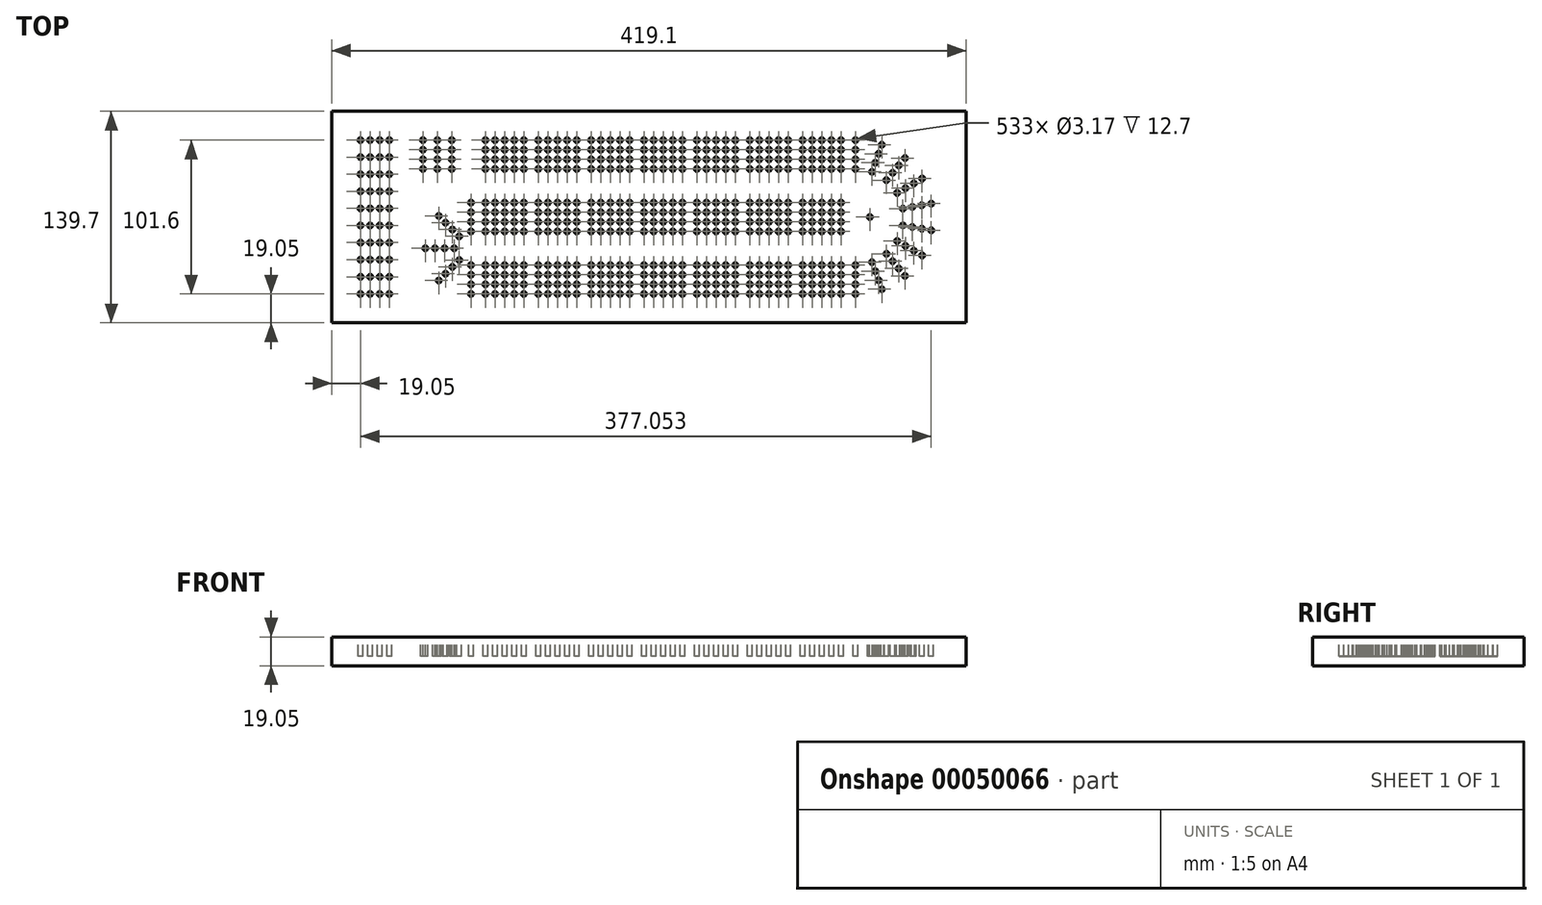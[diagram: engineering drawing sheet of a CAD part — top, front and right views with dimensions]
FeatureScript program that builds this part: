
annotation { "Feature Type Name" : "Feature", "Feature Type Description" : "" }
export const myFeature = defineFeature(function(context is Context, id is Id, definition is map)
    precondition{}
    {
        {
            var Q0;
            Q0=qCreatedBy(makeId("Top.planeOp"),FACE);
            var sketch = newSketch(context, id + "F0", { "sketchPlane" : qUnion([Q0])});
            skLineSegment(sketch, "E0.bottom", {"start": v(0, 0) * mm, "end": v(419.1, 0) * mm});
            skLineSegment(sketch, "E0.top", {"start": v(0, 139.7) * mm, "end": v(419.1, 139.7) * mm});
            skLineSegment(sketch, "E0.left", {"start": v(0, 0) * mm, "end": v(0, 139.7) * mm});
            skLineSegment(sketch, "E0.right", {"start": v(419.1, 0) * mm, "end": v(419.1, 139.7) * mm});
            skSolve(sketch);
        }
        {
            var Q0;
            Q0 = qSketchRegion(id + "F0", true);
            extrude(context, id + "F1", {"entities" : qUnion([Q0]), "depth" : 19.05 * mm});
        }
        {
            var Q0;
            Q0=makeQuery(id+"F1.opExtrude","CAP_FACE",FACE,{"disambiguationData":[OSD([sQuery(id+"F0.wireOp",EDGE,"E0.bottom"),sQuery(id+"F0.wireOp",EDGE,"E0.top"),sQuery(id+"F0.wireOp",EDGE,"E0.left"),sQuery(id+"F0.wireOp",EDGE,"E0.right")])],"isStart":false});
            var sketch = newSketch(context, id + "F2", { "sketchPlane" : qUnion([Q0])});
            skLineSegment(sketch, "E1", {"start": v(19.05, 139.7) * mm, "end": v(19.05, 120.65) * mm});
            skLineSegment(sketch, "E2", {"start": v(19.05, 120.65) * mm, "end": v(0, 120.65) * mm});
            skCircle(sketch, "E3", {"center": v(19.05, 120.65) * mm, "radius": 1.59 * mm});
            skCircle(sketch, "E4.0.1.0", {"center": v(19.05, 109.36) * mm, "radius": 1.59 * mm});
            skCircle(sketch, "E4.0.2.0", {"center": v(19.05, 98.07) * mm, "radius": 1.59 * mm});
            skCircle(sketch, "E4.0.3.0", {"center": v(19.05, 86.78) * mm, "radius": 1.59 * mm});
            skCircle(sketch, "E4.0.4.0", {"center": v(19.05, 75.5) * mm, "radius": 1.59 * mm});
            skCircle(sketch, "E4.0.5.0", {"center": v(19.05, 64.2) * mm, "radius": 1.59 * mm});
            skCircle(sketch, "E4.0.6.0", {"center": v(19.05, 52.92) * mm, "radius": 1.59 * mm});
            skCircle(sketch, "E4.0.7.0", {"center": v(19.05, 41.63) * mm, "radius": 1.59 * mm});
            skCircle(sketch, "E4.0.8.0", {"center": v(19.05, 30.34) * mm, "radius": 1.59 * mm});
            skCircle(sketch, "E4.0.9.0", {"center": v(19.05, 19.05) * mm, "radius": 1.59 * mm});
            skCircle(sketch, "E4.1.0.0", {"center": v(25.4, 120.65) * mm, "radius": 1.59 * mm});
            skCircle(sketch, "E4.1.1.0", {"center": v(25.4, 109.36) * mm, "radius": 1.59 * mm});
            skCircle(sketch, "E4.1.2.0", {"center": v(25.4, 98.07) * mm, "radius": 1.59 * mm});
            skCircle(sketch, "E4.1.3.0", {"center": v(25.4, 86.78) * mm, "radius": 1.59 * mm});
            skCircle(sketch, "E4.1.4.0", {"center": v(25.4, 75.5) * mm, "radius": 1.59 * mm});
            skCircle(sketch, "E4.1.5.0", {"center": v(25.4, 64.2) * mm, "radius": 1.59 * mm});
            skCircle(sketch, "E4.1.6.0", {"center": v(25.4, 52.92) * mm, "radius": 1.59 * mm});
            skCircle(sketch, "E4.1.7.0", {"center": v(25.4, 41.63) * mm, "radius": 1.59 * mm});
            skCircle(sketch, "E4.1.8.0", {"center": v(25.4, 30.34) * mm, "radius": 1.59 * mm});
            skCircle(sketch, "E4.1.9.0", {"center": v(25.4, 19.05) * mm, "radius": 1.59 * mm});
            skCircle(sketch, "E4.2.0.0", {"center": v(31.75, 120.65) * mm, "radius": 1.59 * mm});
            skCircle(sketch, "E4.2.1.0", {"center": v(31.75, 109.36) * mm, "radius": 1.59 * mm});
            skCircle(sketch, "E4.2.2.0", {"center": v(31.75, 98.07) * mm, "radius": 1.59 * mm});
            skCircle(sketch, "E4.2.3.0", {"center": v(31.75, 86.78) * mm, "radius": 1.59 * mm});
            skCircle(sketch, "E4.2.4.0", {"center": v(31.75, 75.5) * mm, "radius": 1.59 * mm});
            skCircle(sketch, "E4.2.5.0", {"center": v(31.75, 64.2) * mm, "radius": 1.59 * mm});
            skCircle(sketch, "E4.2.6.0", {"center": v(31.75, 52.92) * mm, "radius": 1.59 * mm});
            skCircle(sketch, "E4.2.7.0", {"center": v(31.75, 41.63) * mm, "radius": 1.59 * mm});
            skCircle(sketch, "E4.2.8.0", {"center": v(31.75, 30.34) * mm, "radius": 1.59 * mm});
            skCircle(sketch, "E4.2.9.0", {"center": v(31.75, 19.05) * mm, "radius": 1.59 * mm});
            skCircle(sketch, "E4.3.0.0", {"center": v(38.1, 120.65) * mm, "radius": 1.59 * mm});
            skCircle(sketch, "E4.3.1.0", {"center": v(38.1, 109.36) * mm, "radius": 1.59 * mm});
            skCircle(sketch, "E4.3.2.0", {"center": v(38.1, 98.07) * mm, "radius": 1.59 * mm});
            skCircle(sketch, "E4.3.3.0", {"center": v(38.1, 86.78) * mm, "radius": 1.59 * mm});
            skCircle(sketch, "E4.3.4.0", {"center": v(38.1, 75.5) * mm, "radius": 1.59 * mm});
            skCircle(sketch, "E4.3.5.0", {"center": v(38.1, 64.2) * mm, "radius": 1.59 * mm});
            skCircle(sketch, "E4.3.6.0", {"center": v(38.1, 52.92) * mm, "radius": 1.59 * mm});
            skCircle(sketch, "E4.3.7.0", {"center": v(38.1, 41.63) * mm, "radius": 1.59 * mm});
            skCircle(sketch, "E4.3.8.0", {"center": v(38.1, 30.34) * mm, "radius": 1.59 * mm});
            skCircle(sketch, "E4.3.9.0", {"center": v(38.1, 19.05) * mm, "radius": 1.59 * mm});
            skLineSegment(sketch, "E4.direction1", {"start": v(19.05, 120.65) * mm, "end": v(25.4, 120.65) * mm, "construction": true});
            skLineSegment(sketch, "E4.direction2", {"start": v(19.05, 120.65) * mm, "end": v(19.05, 109.36) * mm, "construction": true});
            skCircle(sketch, "E5", {"center": v(60.32, 120.65) * mm, "radius": 1.59 * mm});
            skCircle(sketch, "E6.0.1.0", {"center": v(60.32, 114.3) * mm, "radius": 1.59 * mm});
            skCircle(sketch, "E6.0.2.0", {"center": v(60.32, 107.95) * mm, "radius": 1.59 * mm});
            skCircle(sketch, "E6.0.3.0", {"center": v(60.32, 101.6) * mm, "radius": 1.59 * mm});
            skCircle(sketch, "E6.1.0.0", {"center": v(69.85, 120.65) * mm, "radius": 1.59 * mm});
            skCircle(sketch, "E6.1.1.0", {"center": v(69.85, 114.3) * mm, "radius": 1.59 * mm});
            skCircle(sketch, "E6.1.2.0", {"center": v(69.85, 107.95) * mm, "radius": 1.59 * mm});
            skCircle(sketch, "E6.1.3.0", {"center": v(69.85, 101.6) * mm, "radius": 1.59 * mm});
            skCircle(sketch, "E6.2.0.0", {"center": v(79.38, 120.65) * mm, "radius": 1.59 * mm});
            skCircle(sketch, "E6.2.1.0", {"center": v(79.38, 114.3) * mm, "radius": 1.59 * mm});
            skCircle(sketch, "E6.2.2.0", {"center": v(79.38, 107.95) * mm, "radius": 1.59 * mm});
            skCircle(sketch, "E6.2.3.0", {"center": v(79.38, 101.6) * mm, "radius": 1.59 * mm});
            skLineSegment(sketch, "E6.direction1", {"start": v(60.32, 120.65) * mm, "end": v(69.85, 120.65) * mm, "construction": true});
            skLineSegment(sketch, "E6.direction2", {"start": v(60.32, 120.65) * mm, "end": v(60.32, 114.3) * mm, "construction": true});
            skCircle(sketch, "E7", {"center": v(101.6, 120.65) * mm, "radius": 1.59 * mm});
            skCircle(sketch, "E8.0.1.0", {"center": v(101.6, 114.3) * mm, "radius": 1.59 * mm});
            skCircle(sketch, "E8.0.2.0", {"center": v(101.6, 107.95) * mm, "radius": 1.59 * mm});
            skCircle(sketch, "E8.0.3.0", {"center": v(101.6, 101.6) * mm, "radius": 1.59 * mm});
            skCircle(sketch, "E8.1.0.0", {"center": v(107.95, 120.65) * mm, "radius": 1.59 * mm});
            skCircle(sketch, "E8.1.1.0", {"center": v(107.95, 114.3) * mm, "radius": 1.59 * mm});
            skCircle(sketch, "E8.1.2.0", {"center": v(107.95, 107.95) * mm, "radius": 1.59 * mm});
            skCircle(sketch, "E8.1.3.0", {"center": v(107.95, 101.6) * mm, "radius": 1.59 * mm});
            skCircle(sketch, "E8.2.0.0", {"center": v(114.3, 120.65) * mm, "radius": 1.59 * mm});
            skCircle(sketch, "E8.2.1.0", {"center": v(114.3, 114.3) * mm, "radius": 1.59 * mm});
            skCircle(sketch, "E8.2.2.0", {"center": v(114.3, 107.95) * mm, "radius": 1.59 * mm});
            skCircle(sketch, "E8.2.3.0", {"center": v(114.3, 101.6) * mm, "radius": 1.59 * mm});
            skCircle(sketch, "E8.3.0.0", {"center": v(120.65, 120.65) * mm, "radius": 1.59 * mm});
            skCircle(sketch, "E8.3.1.0", {"center": v(120.65, 114.3) * mm, "radius": 1.59 * mm});
            skCircle(sketch, "E8.3.2.0", {"center": v(120.65, 107.95) * mm, "radius": 1.59 * mm});
            skCircle(sketch, "E8.3.3.0", {"center": v(120.65, 101.6) * mm, "radius": 1.59 * mm});
            skCircle(sketch, "E8.4.0.0", {"center": v(127, 120.65) * mm, "radius": 1.59 * mm});
            skCircle(sketch, "E8.4.1.0", {"center": v(127, 114.3) * mm, "radius": 1.59 * mm});
            skCircle(sketch, "E8.4.2.0", {"center": v(127, 107.95) * mm, "radius": 1.59 * mm});
            skCircle(sketch, "E8.4.3.0", {"center": v(127, 101.6) * mm, "radius": 1.59 * mm});
            skLineSegment(sketch, "E8.direction1", {"start": v(101.6, 120.65) * mm, "end": v(107.95, 120.65) * mm, "construction": true});
            skLineSegment(sketch, "E8.direction2", {"start": v(101.6, 120.65) * mm, "end": v(101.6, 114.3) * mm, "construction": true});
            skCircle(sketch, "E9.1.0.0", {"center": v(149.22, 114.3) * mm, "radius": 1.59 * mm});
            skCircle(sketch, "E9.1.0.1", {"center": v(136.53, 107.95) * mm, "radius": 1.59 * mm});
            skCircle(sketch, "E9.1.0.2", {"center": v(161.92, 107.95) * mm, "radius": 1.59 * mm});
            skCircle(sketch, "E9.1.0.3", {"center": v(149.22, 120.65) * mm, "radius": 1.59 * mm});
            skCircle(sketch, "E9.1.0.4", {"center": v(161.92, 114.3) * mm, "radius": 1.59 * mm});
            skCircle(sketch, "E9.1.0.5", {"center": v(161.92, 120.65) * mm, "radius": 1.59 * mm});
            skCircle(sketch, "E9.1.0.6", {"center": v(142.88, 101.6) * mm, "radius": 1.59 * mm});
            skCircle(sketch, "E9.1.0.7", {"center": v(155.57, 107.95) * mm, "radius": 1.59 * mm});
            skCircle(sketch, "E9.1.0.8", {"center": v(142.88, 107.95) * mm, "radius": 1.59 * mm});
            skCircle(sketch, "E9.1.0.9", {"center": v(155.57, 101.6) * mm, "radius": 1.59 * mm});
            skCircle(sketch, "E9.1.0.10", {"center": v(155.57, 114.3) * mm, "radius": 1.59 * mm});
            skCircle(sketch, "E9.1.0.11", {"center": v(149.22, 107.95) * mm, "radius": 1.59 * mm});
            skCircle(sketch, "E9.1.0.12", {"center": v(149.22, 101.6) * mm, "radius": 1.59 * mm});
            skCircle(sketch, "E9.1.0.13", {"center": v(161.92, 101.6) * mm, "radius": 1.59 * mm});
            skCircle(sketch, "E9.1.0.14", {"center": v(136.53, 101.6) * mm, "radius": 1.59 * mm});
            skCircle(sketch, "E9.1.0.15", {"center": v(155.57, 120.65) * mm, "radius": 1.59 * mm});
            skCircle(sketch, "E9.1.0.16", {"center": v(142.88, 114.3) * mm, "radius": 1.59 * mm});
            skCircle(sketch, "E9.1.0.17", {"center": v(136.53, 114.3) * mm, "radius": 1.59 * mm});
            skCircle(sketch, "E9.1.0.18", {"center": v(142.88, 120.65) * mm, "radius": 1.59 * mm});
            skLineSegment(sketch, "E9.1.0.19", {"start": v(136.53, 120.65) * mm, "end": v(136.53, 114.3) * mm, "construction": true});
            skCircle(sketch, "E9.1.0.20", {"center": v(136.53, 120.65) * mm, "radius": 1.59 * mm});
            skLineSegment(sketch, "E9.1.0.21", {"start": v(136.53, 120.65) * mm, "end": v(142.87, 120.65) * mm, "construction": true});
            skCircle(sketch, "E9.2.0.0", {"center": v(184.15, 114.3) * mm, "radius": 1.59 * mm});
            skCircle(sketch, "E9.2.0.1", {"center": v(171.45, 107.95) * mm, "radius": 1.59 * mm});
            skCircle(sketch, "E9.2.0.2", {"center": v(196.85, 107.95) * mm, "radius": 1.59 * mm});
            skCircle(sketch, "E9.2.0.3", {"center": v(184.15, 120.65) * mm, "radius": 1.59 * mm});
            skCircle(sketch, "E9.2.0.4", {"center": v(196.85, 114.3) * mm, "radius": 1.59 * mm});
            skCircle(sketch, "E9.2.0.5", {"center": v(196.85, 120.65) * mm, "radius": 1.59 * mm});
            skCircle(sketch, "E9.2.0.6", {"center": v(177.8, 101.6) * mm, "radius": 1.59 * mm});
            skCircle(sketch, "E9.2.0.7", {"center": v(190.5, 107.95) * mm, "radius": 1.59 * mm});
            skCircle(sketch, "E9.2.0.8", {"center": v(177.8, 107.95) * mm, "radius": 1.59 * mm});
            skCircle(sketch, "E9.2.0.9", {"center": v(190.5, 101.6) * mm, "radius": 1.59 * mm});
            skCircle(sketch, "E9.2.0.10", {"center": v(190.5, 114.3) * mm, "radius": 1.59 * mm});
            skCircle(sketch, "E9.2.0.11", {"center": v(184.15, 107.95) * mm, "radius": 1.59 * mm});
            skCircle(sketch, "E9.2.0.12", {"center": v(184.15, 101.6) * mm, "radius": 1.59 * mm});
            skCircle(sketch, "E9.2.0.13", {"center": v(196.85, 101.6) * mm, "radius": 1.59 * mm});
            skCircle(sketch, "E9.2.0.14", {"center": v(171.45, 101.6) * mm, "radius": 1.59 * mm});
            skCircle(sketch, "E9.2.0.15", {"center": v(190.5, 120.65) * mm, "radius": 1.59 * mm});
            skCircle(sketch, "E9.2.0.16", {"center": v(177.8, 114.3) * mm, "radius": 1.59 * mm});
            skCircle(sketch, "E9.2.0.17", {"center": v(171.45, 114.3) * mm, "radius": 1.59 * mm});
            skCircle(sketch, "E9.2.0.18", {"center": v(177.8, 120.65) * mm, "radius": 1.59 * mm});
            skLineSegment(sketch, "E9.2.0.19", {"start": v(171.45, 120.65) * mm, "end": v(171.45, 114.3) * mm, "construction": true});
            skCircle(sketch, "E9.2.0.20", {"center": v(171.45, 120.65) * mm, "radius": 1.59 * mm});
            skLineSegment(sketch, "E9.2.0.21", {"start": v(171.45, 120.65) * mm, "end": v(177.8, 120.65) * mm, "construction": true});
            skCircle(sketch, "E9.3.0.0", {"center": v(219.08, 114.3) * mm, "radius": 1.59 * mm});
            skCircle(sketch, "E9.3.0.1", {"center": v(206.38, 107.95) * mm, "radius": 1.59 * mm});
            skCircle(sketch, "E9.3.0.2", {"center": v(231.78, 107.95) * mm, "radius": 1.59 * mm});
            skCircle(sketch, "E9.3.0.3", {"center": v(219.08, 120.65) * mm, "radius": 1.59 * mm});
            skCircle(sketch, "E9.3.0.4", {"center": v(231.78, 114.3) * mm, "radius": 1.59 * mm});
            skCircle(sketch, "E9.3.0.5", {"center": v(231.78, 120.65) * mm, "radius": 1.59 * mm});
            skCircle(sketch, "E9.3.0.6", {"center": v(212.73, 101.6) * mm, "radius": 1.59 * mm});
            skCircle(sketch, "E9.3.0.7", {"center": v(225.43, 107.95) * mm, "radius": 1.59 * mm});
            skCircle(sketch, "E9.3.0.8", {"center": v(212.73, 107.95) * mm, "radius": 1.59 * mm});
            skCircle(sketch, "E9.3.0.9", {"center": v(225.43, 101.6) * mm, "radius": 1.59 * mm});
            skCircle(sketch, "E9.3.0.10", {"center": v(225.43, 114.3) * mm, "radius": 1.59 * mm});
            skCircle(sketch, "E9.3.0.11", {"center": v(219.08, 107.95) * mm, "radius": 1.59 * mm});
            skCircle(sketch, "E9.3.0.12", {"center": v(219.08, 101.6) * mm, "radius": 1.59 * mm});
            skCircle(sketch, "E9.3.0.13", {"center": v(231.78, 101.6) * mm, "radius": 1.59 * mm});
            skCircle(sketch, "E9.3.0.14", {"center": v(206.38, 101.6) * mm, "radius": 1.59 * mm});
            skCircle(sketch, "E9.3.0.15", {"center": v(225.43, 120.65) * mm, "radius": 1.59 * mm});
            skCircle(sketch, "E9.3.0.16", {"center": v(212.73, 114.3) * mm, "radius": 1.59 * mm});
            skCircle(sketch, "E9.3.0.17", {"center": v(206.38, 114.3) * mm, "radius": 1.59 * mm});
            skCircle(sketch, "E9.3.0.18", {"center": v(212.73, 120.65) * mm, "radius": 1.59 * mm});
            skLineSegment(sketch, "E9.3.0.19", {"start": v(206.38, 120.65) * mm, "end": v(206.38, 114.3) * mm, "construction": true});
            skCircle(sketch, "E9.3.0.20", {"center": v(206.38, 120.65) * mm, "radius": 1.59 * mm});
            skLineSegment(sketch, "E9.3.0.21", {"start": v(206.38, 120.65) * mm, "end": v(212.72, 120.65) * mm, "construction": true});
            skCircle(sketch, "E9.4.0.0", {"center": v(254, 114.3) * mm, "radius": 1.59 * mm});
            skCircle(sketch, "E9.4.0.1", {"center": v(241.3, 107.95) * mm, "radius": 1.59 * mm});
            skCircle(sketch, "E9.4.0.2", {"center": v(266.7, 107.95) * mm, "radius": 1.59 * mm});
            skCircle(sketch, "E9.4.0.3", {"center": v(254, 120.65) * mm, "radius": 1.59 * mm});
            skCircle(sketch, "E9.4.0.4", {"center": v(266.7, 114.3) * mm, "radius": 1.59 * mm});
            skCircle(sketch, "E9.4.0.5", {"center": v(266.7, 120.65) * mm, "radius": 1.59 * mm});
            skCircle(sketch, "E9.4.0.6", {"center": v(247.65, 101.6) * mm, "radius": 1.59 * mm});
            skCircle(sketch, "E9.4.0.7", {"center": v(260.35, 107.95) * mm, "radius": 1.59 * mm});
            skCircle(sketch, "E9.4.0.8", {"center": v(247.65, 107.95) * mm, "radius": 1.59 * mm});
            skCircle(sketch, "E9.4.0.9", {"center": v(260.35, 101.6) * mm, "radius": 1.59 * mm});
            skCircle(sketch, "E9.4.0.10", {"center": v(260.35, 114.3) * mm, "radius": 1.59 * mm});
            skCircle(sketch, "E9.4.0.11", {"center": v(254, 107.95) * mm, "radius": 1.59 * mm});
            skCircle(sketch, "E9.4.0.12", {"center": v(254, 101.6) * mm, "radius": 1.59 * mm});
            skCircle(sketch, "E9.4.0.13", {"center": v(266.7, 101.6) * mm, "radius": 1.59 * mm});
            skCircle(sketch, "E9.4.0.14", {"center": v(241.3, 101.6) * mm, "radius": 1.59 * mm});
            skCircle(sketch, "E9.4.0.15", {"center": v(260.35, 120.65) * mm, "radius": 1.59 * mm});
            skCircle(sketch, "E9.4.0.16", {"center": v(247.65, 114.3) * mm, "radius": 1.59 * mm});
            skCircle(sketch, "E9.4.0.17", {"center": v(241.3, 114.3) * mm, "radius": 1.59 * mm});
            skCircle(sketch, "E9.4.0.18", {"center": v(247.65, 120.65) * mm, "radius": 1.59 * mm});
            skLineSegment(sketch, "E9.4.0.19", {"start": v(241.3, 120.65) * mm, "end": v(241.3, 114.3) * mm, "construction": true});
            skCircle(sketch, "E9.4.0.20", {"center": v(241.3, 120.65) * mm, "radius": 1.59 * mm});
            skLineSegment(sketch, "E9.4.0.21", {"start": v(241.3, 120.65) * mm, "end": v(247.65, 120.65) * mm, "construction": true});
            skLineSegment(sketch, "E9.direction1", {"start": v(114.3, 114.3) * mm, "end": v(149.22, 114.3) * mm, "construction": true});
            skCircle(sketch, "E10.0.5.0", {"center": v(288.93, 114.3) * mm, "radius": 1.59 * mm});
            skCircle(sketch, "E10.2.5.0", {"center": v(276.23, 107.95) * mm, "radius": 1.59 * mm});
            skCircle(sketch, "E10.4.5.0", {"center": v(301.63, 107.95) * mm, "radius": 1.59 * mm});
            skCircle(sketch, "E10.6.5.0", {"center": v(288.93, 120.65) * mm, "radius": 1.59 * mm});
            skCircle(sketch, "E10.8.5.0", {"center": v(301.63, 114.3) * mm, "radius": 1.59 * mm});
            skCircle(sketch, "E10.10.5.0", {"center": v(301.63, 120.65) * mm, "radius": 1.59 * mm});
            skCircle(sketch, "E10.12.5.0", {"center": v(282.58, 101.6) * mm, "radius": 1.59 * mm});
            skCircle(sketch, "E10.14.5.0", {"center": v(295.28, 107.95) * mm, "radius": 1.59 * mm});
            skCircle(sketch, "E10.16.5.0", {"center": v(282.58, 107.95) * mm, "radius": 1.59 * mm});
            skCircle(sketch, "E10.18.5.0", {"center": v(295.28, 101.6) * mm, "radius": 1.59 * mm});
            skCircle(sketch, "E10.20.5.0", {"center": v(295.28, 114.3) * mm, "radius": 1.59 * mm});
            skCircle(sketch, "E10.22.5.0", {"center": v(288.93, 107.95) * mm, "radius": 1.59 * mm});
            skCircle(sketch, "E10.24.5.0", {"center": v(288.93, 101.6) * mm, "radius": 1.59 * mm});
            skCircle(sketch, "E10.26.5.0", {"center": v(301.63, 101.6) * mm, "radius": 1.59 * mm});
            skCircle(sketch, "E10.28.5.0", {"center": v(276.23, 101.6) * mm, "radius": 1.59 * mm});
            skCircle(sketch, "E10.30.5.0", {"center": v(295.28, 120.65) * mm, "radius": 1.59 * mm});
            skCircle(sketch, "E10.32.5.0", {"center": v(282.58, 114.3) * mm, "radius": 1.59 * mm});
            skCircle(sketch, "E10.34.5.0", {"center": v(276.23, 114.3) * mm, "radius": 1.59 * mm});
            skCircle(sketch, "E10.36.5.0", {"center": v(282.58, 120.65) * mm, "radius": 1.59 * mm});
            skLineSegment(sketch, "E10.38.5.0", {"start": v(276.23, 120.65) * mm, "end": v(276.23, 114.3) * mm, "construction": true});
            skCircle(sketch, "E10.41.5.0", {"center": v(276.23, 120.65) * mm, "radius": 1.59 * mm});
            skLineSegment(sketch, "E10.43.5.0", {"start": v(276.23, 120.65) * mm, "end": v(282.58, 120.65) * mm, "construction": true});
            skCircle(sketch, "E10.0.6.0", {"center": v(323.85, 114.3) * mm, "radius": 1.59 * mm});
            skCircle(sketch, "E10.2.6.0", {"center": v(311.15, 107.95) * mm, "radius": 1.59 * mm});
            skCircle(sketch, "E10.4.6.0", {"center": v(336.55, 107.95) * mm, "radius": 1.59 * mm});
            skCircle(sketch, "E10.6.6.0", {"center": v(323.85, 120.65) * mm, "radius": 1.59 * mm});
            skCircle(sketch, "E10.8.6.0", {"center": v(336.55, 114.3) * mm, "radius": 1.59 * mm});
            skCircle(sketch, "E10.10.6.0", {"center": v(336.55, 120.65) * mm, "radius": 1.59 * mm});
            skCircle(sketch, "E10.12.6.0", {"center": v(317.5, 101.6) * mm, "radius": 1.59 * mm});
            skCircle(sketch, "E10.14.6.0", {"center": v(330.2, 107.95) * mm, "radius": 1.59 * mm});
            skCircle(sketch, "E10.16.6.0", {"center": v(317.5, 107.95) * mm, "radius": 1.59 * mm});
            skCircle(sketch, "E10.18.6.0", {"center": v(330.2, 101.6) * mm, "radius": 1.59 * mm});
            skCircle(sketch, "E10.20.6.0", {"center": v(330.2, 114.3) * mm, "radius": 1.59 * mm});
            skCircle(sketch, "E10.22.6.0", {"center": v(323.85, 107.95) * mm, "radius": 1.59 * mm});
            skCircle(sketch, "E10.24.6.0", {"center": v(323.85, 101.6) * mm, "radius": 1.59 * mm});
            skCircle(sketch, "E10.26.6.0", {"center": v(336.55, 101.6) * mm, "radius": 1.59 * mm});
            skCircle(sketch, "E10.28.6.0", {"center": v(311.15, 101.6) * mm, "radius": 1.59 * mm});
            skCircle(sketch, "E10.30.6.0", {"center": v(330.2, 120.65) * mm, "radius": 1.59 * mm});
            skCircle(sketch, "E10.32.6.0", {"center": v(317.5, 114.3) * mm, "radius": 1.59 * mm});
            skCircle(sketch, "E10.34.6.0", {"center": v(311.15, 114.3) * mm, "radius": 1.59 * mm});
            skCircle(sketch, "E10.36.6.0", {"center": v(317.5, 120.65) * mm, "radius": 1.59 * mm});
            skLineSegment(sketch, "E10.38.6.0", {"start": v(311.15, 120.65) * mm, "end": v(311.15, 114.3) * mm, "construction": true});
            skCircle(sketch, "E10.41.6.0", {"center": v(311.15, 120.65) * mm, "radius": 1.59 * mm});
            skLineSegment(sketch, "E10.43.6.0", {"start": v(311.15, 120.65) * mm, "end": v(317.5, 120.65) * mm, "construction": true});
            skCircle(sketch, "E11.0.1.0", {"center": v(219.08, 66.68) * mm, "radius": 1.59 * mm});
            skCircle(sketch, "E11.0.1.1", {"center": v(171.45, 66.68) * mm, "radius": 1.59 * mm});
            skCircle(sketch, "E11.0.1.2", {"center": v(155.57, 66.68) * mm, "radius": 1.59 * mm});
            skCircle(sketch, "E11.0.1.3", {"center": v(317.5, 66.68) * mm, "radius": 1.59 * mm});
            skCircle(sketch, "E11.0.1.4", {"center": v(276.23, 60.33) * mm, "radius": 1.59 * mm});
            skCircle(sketch, "E11.0.1.5", {"center": v(266.7, 79.38) * mm, "radius": 1.59 * mm});
            skCircle(sketch, "E11.0.1.6", {"center": v(155.57, 60.33) * mm, "radius": 1.59 * mm});
            skCircle(sketch, "E11.0.1.7", {"center": v(120.65, 60.33) * mm, "radius": 1.59 * mm});
            skCircle(sketch, "E11.0.1.8", {"center": v(260.35, 66.68) * mm, "radius": 1.59 * mm});
            skCircle(sketch, "E11.0.1.9", {"center": v(231.78, 60.33) * mm, "radius": 1.59 * mm});
            skCircle(sketch, "E11.0.1.10", {"center": v(184.15, 79.38) * mm, "radius": 1.59 * mm});
            skCircle(sketch, "E11.0.1.11", {"center": v(330.2, 73.03) * mm, "radius": 1.59 * mm});
            skCircle(sketch, "E11.0.1.12", {"center": v(282.58, 73.03) * mm, "radius": 1.59 * mm});
            skCircle(sketch, "E11.0.1.13", {"center": v(288.93, 73.03) * mm, "radius": 1.59 * mm});
            skCircle(sketch, "E11.0.1.14", {"center": v(120.65, 66.68) * mm, "radius": 1.59 * mm});
            skCircle(sketch, "E11.0.1.15", {"center": v(219.08, 60.33) * mm, "radius": 1.59 * mm});
            skCircle(sketch, "E11.0.1.16", {"center": v(196.85, 66.68) * mm, "radius": 1.59 * mm});
            skCircle(sketch, "E11.0.1.17", {"center": v(142.88, 66.68) * mm, "radius": 1.59 * mm});
            skCircle(sketch, "E11.0.1.18", {"center": v(330.2, 60.33) * mm, "radius": 1.59 * mm});
            skCircle(sketch, "E11.0.1.19", {"center": v(295.28, 79.38) * mm, "radius": 1.59 * mm});
            skCircle(sketch, "E11.0.1.20", {"center": v(155.57, 73.03) * mm, "radius": 1.59 * mm});
            skCircle(sketch, "E11.0.1.21", {"center": v(206.38, 60.33) * mm, "radius": 1.59 * mm});
            skCircle(sketch, "E11.0.1.22", {"center": v(196.85, 73.03) * mm, "radius": 1.59 * mm});
            skCircle(sketch, "E11.0.1.23", {"center": v(323.85, 66.68) * mm, "radius": 1.59 * mm});
            skCircle(sketch, "E11.0.1.24", {"center": v(276.23, 66.68) * mm, "radius": 1.59 * mm});
            skCircle(sketch, "E11.0.1.25", {"center": v(149.22, 66.68) * mm, "radius": 1.59 * mm});
            skCircle(sketch, "E11.0.1.26", {"center": v(260.35, 60.33) * mm, "radius": 1.59 * mm});
            skCircle(sketch, "E11.0.1.27", {"center": v(196.85, 79.38) * mm, "radius": 1.59 * mm});
            skCircle(sketch, "E11.0.1.28", {"center": v(323.85, 60.33) * mm, "radius": 1.59 * mm});
            skCircle(sketch, "E11.0.1.29", {"center": v(301.63, 66.68) * mm, "radius": 1.59 * mm});
            skCircle(sketch, "E11.0.1.30", {"center": v(149.22, 60.33) * mm, "radius": 1.59 * mm});
            skCircle(sketch, "E11.0.1.31", {"center": v(127, 66.68) * mm, "radius": 1.59 * mm});
            skCircle(sketch, "E11.0.1.32", {"center": v(101.6, 66.68) * mm, "radius": 1.59 * mm});
            skCircle(sketch, "E11.0.1.33", {"center": v(177.8, 60.33) * mm, "radius": 1.59 * mm});
            skCircle(sketch, "E11.0.1.34", {"center": v(336.55, 60.33) * mm, "radius": 1.59 * mm});
            skCircle(sketch, "E11.0.1.35", {"center": v(288.93, 79.38) * mm, "radius": 1.59 * mm});
            skCircle(sketch, "E11.0.1.36", {"center": v(254, 66.68) * mm, "radius": 1.59 * mm});
            skCircle(sketch, "E11.0.1.37", {"center": v(206.38, 66.68) * mm, "radius": 1.59 * mm});
            skCircle(sketch, "E11.0.1.38", {"center": v(190.5, 66.68) * mm, "radius": 1.59 * mm});
            skCircle(sketch, "E11.0.1.39", {"center": v(311.15, 60.33) * mm, "radius": 1.59 * mm});
            skCircle(sketch, "E11.0.1.40", {"center": v(161.92, 60.33) * mm, "radius": 1.59 * mm});
            skCircle(sketch, "E11.0.1.41", {"center": v(127, 60.33) * mm, "radius": 1.59 * mm});
            skCircle(sketch, "E11.0.1.42", {"center": v(101.6, 60.33) * mm, "radius": 1.59 * mm});
            skCircle(sketch, "E11.0.1.43", {"center": v(330.2, 79.38) * mm, "radius": 1.59 * mm});
            skCircle(sketch, "E11.0.1.44", {"center": v(301.63, 79.38) * mm, "radius": 1.59 * mm});
            skCircle(sketch, "E11.0.1.45", {"center": v(136.53, 60.33) * mm, "radius": 1.59 * mm});
            skCircle(sketch, "E11.0.1.46", {"center": v(254, 60.33) * mm, "radius": 1.59 * mm});
            skCircle(sketch, "E11.0.1.47", {"center": v(231.78, 66.68) * mm, "radius": 1.59 * mm});
            skCircle(sketch, "E11.0.1.48", {"center": v(177.8, 66.68) * mm, "radius": 1.59 * mm});
            skCircle(sketch, "E11.0.1.49", {"center": v(155.57, 79.38) * mm, "radius": 1.59 * mm});
            skCircle(sketch, "E11.0.1.50", {"center": v(266.7, 60.33) * mm, "radius": 1.59 * mm});
            skCircle(sketch, "E11.0.1.51", {"center": v(219.08, 79.38) * mm, "radius": 1.59 * mm});
            skCircle(sketch, "E11.0.1.52", {"center": v(190.5, 60.33) * mm, "radius": 1.59 * mm});
            skCircle(sketch, "E11.0.1.53", {"center": v(282.58, 60.33) * mm, "radius": 1.59 * mm});
            skCircle(sketch, "E11.0.1.54", {"center": v(241.3, 60.33) * mm, "radius": 1.59 * mm});
            skCircle(sketch, "E11.0.1.55", {"center": v(231.78, 73.03) * mm, "radius": 1.59 * mm});
            skCircle(sketch, "E11.0.1.56", {"center": v(190.5, 73.03) * mm, "radius": 1.59 * mm});
            skCircle(sketch, "E11.0.1.57", {"center": v(311.15, 66.68) * mm, "radius": 1.59 * mm});
            skCircle(sketch, "E11.0.1.58", {"center": v(295.28, 66.68) * mm, "radius": 1.59 * mm});
            skCircle(sketch, "E11.0.1.59", {"center": v(136.53, 66.68) * mm, "radius": 1.59 * mm});
            skCircle(sketch, "E11.0.1.60", {"center": v(107.95, 60.33) * mm, "radius": 1.59 * mm});
            skCircle(sketch, "E11.0.1.61", {"center": v(260.35, 79.38) * mm, "radius": 1.59 * mm});
            skCircle(sketch, "E11.0.1.62", {"center": v(231.78, 79.38) * mm, "radius": 1.59 * mm});
            skCircle(sketch, "E11.0.1.63", {"center": v(184.15, 66.68) * mm, "radius": 1.59 * mm});
            skCircle(sketch, "E11.0.1.64", {"center": v(336.55, 66.68) * mm, "radius": 1.59 * mm});
            skCircle(sketch, "E11.0.1.65", {"center": v(282.58, 66.68) * mm, "radius": 1.59 * mm});
            skCircle(sketch, "E11.0.1.66", {"center": v(161.92, 66.68) * mm, "radius": 1.59 * mm});
            skCircle(sketch, "E11.0.1.67", {"center": v(212.73, 60.33) * mm, "radius": 1.59 * mm});
            skCircle(sketch, "E11.0.1.68", {"center": v(184.15, 60.33) * mm, "radius": 1.59 * mm});
            skCircle(sketch, "E11.0.1.69", {"center": v(323.85, 79.38) * mm, "radius": 1.59 * mm});
            skCircle(sketch, "E11.0.1.70", {"center": v(225.43, 66.68) * mm, "radius": 1.59 * mm});
            skCircle(sketch, "E11.0.1.71", {"center": v(196.85, 60.33) * mm, "radius": 1.59 * mm});
            skCircle(sketch, "E11.0.1.72", {"center": v(149.22, 79.38) * mm, "radius": 1.59 * mm});
            skCircle(sketch, "E11.0.1.73", {"center": v(336.55, 73.03) * mm, "radius": 1.59 * mm});
            skCircle(sketch, "E11.0.1.74", {"center": v(295.28, 73.03) * mm, "radius": 1.59 * mm});
            skCircle(sketch, "E11.0.1.75", {"center": v(241.3, 66.68) * mm, "radius": 1.59 * mm});
            skCircle(sketch, "E11.0.1.76", {"center": v(114.3, 66.68) * mm, "radius": 1.59 * mm});
            skCircle(sketch, "E11.0.1.77", {"center": v(212.73, 66.68) * mm, "radius": 1.59 * mm});
            skCircle(sketch, "E11.0.1.78", {"center": v(171.45, 60.33) * mm, "radius": 1.59 * mm});
            skCircle(sketch, "E11.0.1.79", {"center": v(336.55, 79.38) * mm, "radius": 1.59 * mm});
            skCircle(sketch, "E11.0.1.80", {"center": v(288.93, 66.68) * mm, "radius": 1.59 * mm});
            skCircle(sketch, "E11.0.1.81", {"center": v(266.7, 66.68) * mm, "radius": 1.59 * mm});
            skCircle(sketch, "E11.0.1.82", {"center": v(190.5, 79.38) * mm, "radius": 1.59 * mm});
            skCircle(sketch, "E11.0.1.83", {"center": v(161.92, 79.38) * mm, "radius": 1.59 * mm});
            skCircle(sketch, "E11.0.1.84", {"center": v(317.5, 60.33) * mm, "radius": 1.59 * mm});
            skCircle(sketch, "E11.0.1.85", {"center": v(288.93, 60.33) * mm, "radius": 1.59 * mm});
            skCircle(sketch, "E11.0.1.86", {"center": v(254, 79.38) * mm, "radius": 1.59 * mm});
            skCircle(sketch, "E11.0.1.87", {"center": v(330.2, 66.68) * mm, "radius": 1.59 * mm});
            skCircle(sketch, "E11.0.1.88", {"center": v(301.63, 60.33) * mm, "radius": 1.59 * mm});
            skCircle(sketch, "E11.0.1.89", {"center": v(266.7, 73.03) * mm, "radius": 1.59 * mm});
            skCircle(sketch, "E11.0.1.90", {"center": v(120.65, 73.03) * mm, "radius": 1.59 * mm});
            skCircle(sketch, "E11.0.1.91", {"center": v(171.45, 73.03) * mm, "radius": 1.59 * mm});
            skLineSegment(sketch, "E11.0.1.92", {"start": v(114.3, 73.03) * mm, "end": v(149.22, 73.03) * mm, "construction": true});
            skCircle(sketch, "E11.0.1.93", {"center": v(247.65, 60.33) * mm, "radius": 1.59 * mm});
            skCircle(sketch, "E11.0.1.94", {"center": v(127, 79.38) * mm, "radius": 1.59 * mm});
            skCircle(sketch, "E11.0.1.95", {"center": v(247.65, 66.68) * mm, "radius": 1.59 * mm});
            skCircle(sketch, "E11.0.1.96", {"center": v(127, 73.03) * mm, "radius": 1.59 * mm});
            skCircle(sketch, "E11.0.1.97", {"center": v(225.43, 79.38) * mm, "radius": 1.59 * mm});
            skCircle(sketch, "E11.0.1.98", {"center": v(282.58, 79.38) * mm, "radius": 1.59 * mm});
            skCircle(sketch, "E11.0.1.99", {"center": v(260.35, 73.03) * mm, "radius": 1.59 * mm});
            skCircle(sketch, "E11.0.1.100", {"center": v(212.73, 73.03) * mm, "radius": 1.59 * mm});
            skCircle(sketch, "E11.0.1.101", {"center": v(219.08, 73.03) * mm, "radius": 1.59 * mm});
            skCircle(sketch, "E11.0.1.102", {"center": v(301.63, 73.03) * mm, "radius": 1.59 * mm});
            skCircle(sketch, "E11.0.1.103", {"center": v(212.73, 79.38) * mm, "radius": 1.59 * mm});
            skCircle(sketch, "E11.0.1.104", {"center": v(323.85, 73.03) * mm, "radius": 1.59 * mm});
            skCircle(sketch, "E11.0.1.105", {"center": v(142.88, 73.03) * mm, "radius": 1.59 * mm});
            skCircle(sketch, "E11.0.1.106", {"center": v(149.22, 73.03) * mm, "radius": 1.59 * mm});
            skCircle(sketch, "E11.0.1.107", {"center": v(107.95, 66.68) * mm, "radius": 1.59 * mm});
            skCircle(sketch, "E11.0.1.108", {"center": v(247.65, 73.03) * mm, "radius": 1.59 * mm});
            skCircle(sketch, "E11.0.1.109", {"center": v(254, 73.03) * mm, "radius": 1.59 * mm});
            skCircle(sketch, "E11.0.1.110", {"center": v(295.28, 60.33) * mm, "radius": 1.59 * mm});
            skCircle(sketch, "E11.0.1.111", {"center": v(114.3, 73.03) * mm, "radius": 1.59 * mm});
            skCircle(sketch, "E11.0.1.112", {"center": v(241.3, 73.03) * mm, "radius": 1.59 * mm});
            skCircle(sketch, "E11.0.1.113", {"center": v(161.92, 73.03) * mm, "radius": 1.59 * mm});
            skCircle(sketch, "E11.0.1.114", {"center": v(114.3, 60.33) * mm, "radius": 1.59 * mm});
            skCircle(sketch, "E11.0.1.115", {"center": v(225.43, 60.33) * mm, "radius": 1.59 * mm});
            skCircle(sketch, "E11.0.1.116", {"center": v(120.65, 79.38) * mm, "radius": 1.59 * mm});
            skCircle(sketch, "E11.0.1.117", {"center": v(225.43, 73.03) * mm, "radius": 1.59 * mm});
            skCircle(sketch, "E11.0.1.118", {"center": v(177.8, 73.03) * mm, "radius": 1.59 * mm});
            skCircle(sketch, "E11.0.1.119", {"center": v(184.15, 73.03) * mm, "radius": 1.59 * mm});
            skCircle(sketch, "E11.0.1.120", {"center": v(142.88, 60.33) * mm, "radius": 1.59 * mm});
            skLineSegment(sketch, "E11.0.1.121", {"start": v(171.45, 79.38) * mm, "end": v(171.45, 73.03) * mm, "construction": true});
            skCircle(sketch, "E11.0.1.122", {"center": v(177.8, 79.38) * mm, "radius": 1.59 * mm});
            skCircle(sketch, "E11.0.1.123", {"center": v(171.45, 79.38) * mm, "radius": 1.59 * mm});
            skCircle(sketch, "E11.0.1.124", {"center": v(276.23, 73.03) * mm, "radius": 1.59 * mm});
            skCircle(sketch, "E11.0.1.125", {"center": v(101.6, 73.03) * mm, "radius": 1.59 * mm});
            skLineSegment(sketch, "E11.0.1.126", {"start": v(171.45, 79.38) * mm, "end": v(177.8, 79.38) * mm, "construction": true});
            skLineSegment(sketch, "E11.0.1.127", {"start": v(276.23, 79.38) * mm, "end": v(276.23, 73.03) * mm, "construction": true});
            skCircle(sketch, "E11.0.1.128", {"center": v(206.38, 73.03) * mm, "radius": 1.59 * mm});
            skCircle(sketch, "E11.0.1.129", {"center": v(276.23, 79.38) * mm, "radius": 1.59 * mm});
            skLineSegment(sketch, "E11.0.1.130", {"start": v(276.23, 79.38) * mm, "end": v(282.58, 79.38) * mm, "construction": true});
            skCircle(sketch, "E11.0.1.131", {"center": v(107.95, 79.38) * mm, "radius": 1.59 * mm});
            skCircle(sketch, "E11.0.1.132", {"center": v(107.95, 73.03) * mm, "radius": 1.59 * mm});
            skCircle(sketch, "E11.0.1.133", {"center": v(317.5, 73.03) * mm, "radius": 1.59 * mm});
            skCircle(sketch, "E11.0.1.134", {"center": v(206.38, 79.38) * mm, "radius": 1.59 * mm});
            skCircle(sketch, "E11.0.1.135", {"center": v(311.15, 73.03) * mm, "radius": 1.59 * mm});
            skCircle(sketch, "E11.0.1.136", {"center": v(136.53, 73.03) * mm, "radius": 1.59 * mm});
            skLineSegment(sketch, "E11.0.1.137", {"start": v(206.38, 79.38) * mm, "end": v(212.72, 79.38) * mm, "construction": true});
            skCircle(sketch, "E11.0.1.138", {"center": v(317.5, 79.38) * mm, "radius": 1.59 * mm});
            skCircle(sketch, "E11.0.1.139", {"center": v(142.88, 79.38) * mm, "radius": 1.59 * mm});
            skCircle(sketch, "E11.0.1.140", {"center": v(114.3, 79.38) * mm, "radius": 1.59 * mm});
            skLineSegment(sketch, "E11.0.1.141", {"start": v(311.15, 79.38) * mm, "end": v(311.15, 73.03) * mm, "construction": true});
            skCircle(sketch, "E11.0.1.142", {"center": v(311.15, 79.38) * mm, "radius": 1.59 * mm});
            skCircle(sketch, "E11.0.1.143", {"center": v(247.65, 79.38) * mm, "radius": 1.59 * mm});
            skLineSegment(sketch, "E11.0.1.144", {"start": v(311.15, 79.38) * mm, "end": v(317.5, 79.38) * mm, "construction": true});
            skLineSegment(sketch, "E11.0.1.145", {"start": v(241.3, 79.38) * mm, "end": v(241.3, 73.03) * mm, "construction": true});
            skCircle(sketch, "E11.0.1.146", {"center": v(241.3, 79.38) * mm, "radius": 1.59 * mm});
            skLineSegment(sketch, "E11.0.1.147", {"start": v(241.3, 79.38) * mm, "end": v(247.65, 79.38) * mm, "construction": true});
            skCircle(sketch, "E11.0.1.148", {"center": v(101.6, 79.38) * mm, "radius": 1.59 * mm});
            skLineSegment(sketch, "E11.0.1.149", {"start": v(101.6, 79.38) * mm, "end": v(107.95, 79.38) * mm, "construction": true});
            skLineSegment(sketch, "E11.0.1.150", {"start": v(101.6, 79.38) * mm, "end": v(101.6, 73.03) * mm, "construction": true});
            skLineSegment(sketch, "E11.0.1.151", {"start": v(206.38, 79.38) * mm, "end": v(206.38, 73.03) * mm, "construction": true});
            skLineSegment(sketch, "E11.0.1.152", {"start": v(136.53, 79.38) * mm, "end": v(136.53, 73.03) * mm, "construction": true});
            skCircle(sketch, "E11.0.1.153", {"center": v(136.53, 79.38) * mm, "radius": 1.59 * mm});
            skLineSegment(sketch, "E11.0.1.154", {"start": v(136.53, 79.38) * mm, "end": v(142.87, 79.38) * mm, "construction": true});
            skCircle(sketch, "E11.0.2.0", {"center": v(219.08, 25.4) * mm, "radius": 1.59 * mm});
            skCircle(sketch, "E11.0.2.1", {"center": v(171.45, 25.4) * mm, "radius": 1.59 * mm});
            skCircle(sketch, "E11.0.2.2", {"center": v(155.57, 25.4) * mm, "radius": 1.59 * mm});
            skCircle(sketch, "E11.0.2.3", {"center": v(317.5, 25.4) * mm, "radius": 1.59 * mm});
            skCircle(sketch, "E11.0.2.4", {"center": v(276.23, 19.05) * mm, "radius": 1.59 * mm});
            skCircle(sketch, "E11.0.2.5", {"center": v(266.7, 38.1) * mm, "radius": 1.59 * mm});
            skCircle(sketch, "E11.0.2.6", {"center": v(155.57, 19.05) * mm, "radius": 1.59 * mm});
            skCircle(sketch, "E11.0.2.7", {"center": v(120.65, 19.05) * mm, "radius": 1.59 * mm});
            skCircle(sketch, "E11.0.2.8", {"center": v(260.35, 25.4) * mm, "radius": 1.59 * mm});
            skCircle(sketch, "E11.0.2.9", {"center": v(231.78, 19.05) * mm, "radius": 1.59 * mm});
            skCircle(sketch, "E11.0.2.10", {"center": v(184.15, 38.1) * mm, "radius": 1.59 * mm});
            skCircle(sketch, "E11.0.2.11", {"center": v(330.2, 31.75) * mm, "radius": 1.59 * mm});
            skCircle(sketch, "E11.0.2.12", {"center": v(282.58, 31.75) * mm, "radius": 1.59 * mm});
            skCircle(sketch, "E11.0.2.13", {"center": v(288.93, 31.75) * mm, "radius": 1.59 * mm});
            skCircle(sketch, "E11.0.2.14", {"center": v(120.65, 25.4) * mm, "radius": 1.59 * mm});
            skCircle(sketch, "E11.0.2.15", {"center": v(219.08, 19.05) * mm, "radius": 1.59 * mm});
            skCircle(sketch, "E11.0.2.16", {"center": v(196.85, 25.4) * mm, "radius": 1.59 * mm});
            skCircle(sketch, "E11.0.2.17", {"center": v(142.88, 25.4) * mm, "radius": 1.59 * mm});
            skCircle(sketch, "E11.0.2.18", {"center": v(330.2, 19.05) * mm, "radius": 1.59 * mm});
            skCircle(sketch, "E11.0.2.19", {"center": v(295.28, 38.1) * mm, "radius": 1.59 * mm});
            skCircle(sketch, "E11.0.2.20", {"center": v(155.57, 31.75) * mm, "radius": 1.59 * mm});
            skCircle(sketch, "E11.0.2.21", {"center": v(206.38, 19.05) * mm, "radius": 1.59 * mm});
            skCircle(sketch, "E11.0.2.22", {"center": v(196.85, 31.75) * mm, "radius": 1.59 * mm});
            skCircle(sketch, "E11.0.2.23", {"center": v(323.85, 25.4) * mm, "radius": 1.59 * mm});
            skCircle(sketch, "E11.0.2.24", {"center": v(276.23, 25.4) * mm, "radius": 1.59 * mm});
            skCircle(sketch, "E11.0.2.25", {"center": v(149.22, 25.4) * mm, "radius": 1.59 * mm});
            skCircle(sketch, "E11.0.2.26", {"center": v(260.35, 19.05) * mm, "radius": 1.59 * mm});
            skCircle(sketch, "E11.0.2.27", {"center": v(196.85, 38.1) * mm, "radius": 1.59 * mm});
            skCircle(sketch, "E11.0.2.28", {"center": v(323.85, 19.05) * mm, "radius": 1.59 * mm});
            skCircle(sketch, "E11.0.2.29", {"center": v(301.63, 25.4) * mm, "radius": 1.59 * mm});
            skCircle(sketch, "E11.0.2.30", {"center": v(149.22, 19.05) * mm, "radius": 1.59 * mm});
            skCircle(sketch, "E11.0.2.31", {"center": v(127, 25.4) * mm, "radius": 1.59 * mm});
            skCircle(sketch, "E11.0.2.32", {"center": v(101.6, 25.4) * mm, "radius": 1.59 * mm});
            skCircle(sketch, "E11.0.2.33", {"center": v(177.8, 19.05) * mm, "radius": 1.59 * mm});
            skCircle(sketch, "E11.0.2.34", {"center": v(336.55, 19.05) * mm, "radius": 1.59 * mm});
            skCircle(sketch, "E11.0.2.35", {"center": v(288.93, 38.1) * mm, "radius": 1.59 * mm});
            skCircle(sketch, "E11.0.2.36", {"center": v(254, 25.4) * mm, "radius": 1.59 * mm});
            skCircle(sketch, "E11.0.2.37", {"center": v(206.38, 25.4) * mm, "radius": 1.59 * mm});
            skCircle(sketch, "E11.0.2.38", {"center": v(190.5, 25.4) * mm, "radius": 1.59 * mm});
            skCircle(sketch, "E11.0.2.39", {"center": v(311.15, 19.05) * mm, "radius": 1.59 * mm});
            skCircle(sketch, "E11.0.2.40", {"center": v(161.92, 19.05) * mm, "radius": 1.59 * mm});
            skCircle(sketch, "E11.0.2.41", {"center": v(127, 19.05) * mm, "radius": 1.59 * mm});
            skCircle(sketch, "E11.0.2.42", {"center": v(101.6, 19.05) * mm, "radius": 1.59 * mm});
            skCircle(sketch, "E11.0.2.43", {"center": v(330.2, 38.1) * mm, "radius": 1.59 * mm});
            skCircle(sketch, "E11.0.2.44", {"center": v(301.63, 38.1) * mm, "radius": 1.59 * mm});
            skCircle(sketch, "E11.0.2.45", {"center": v(136.53, 19.05) * mm, "radius": 1.59 * mm});
            skCircle(sketch, "E11.0.2.46", {"center": v(254, 19.05) * mm, "radius": 1.59 * mm});
            skCircle(sketch, "E11.0.2.47", {"center": v(231.78, 25.4) * mm, "radius": 1.59 * mm});
            skCircle(sketch, "E11.0.2.48", {"center": v(177.8, 25.4) * mm, "radius": 1.59 * mm});
            skCircle(sketch, "E11.0.2.49", {"center": v(155.57, 38.1) * mm, "radius": 1.59 * mm});
            skCircle(sketch, "E11.0.2.50", {"center": v(266.7, 19.05) * mm, "radius": 1.59 * mm});
            skCircle(sketch, "E11.0.2.51", {"center": v(219.08, 38.1) * mm, "radius": 1.59 * mm});
            skCircle(sketch, "E11.0.2.52", {"center": v(190.5, 19.05) * mm, "radius": 1.59 * mm});
            skCircle(sketch, "E11.0.2.53", {"center": v(282.58, 19.05) * mm, "radius": 1.59 * mm});
            skCircle(sketch, "E11.0.2.54", {"center": v(241.3, 19.05) * mm, "radius": 1.59 * mm});
            skCircle(sketch, "E11.0.2.55", {"center": v(231.78, 31.75) * mm, "radius": 1.59 * mm});
            skCircle(sketch, "E11.0.2.56", {"center": v(190.5, 31.75) * mm, "radius": 1.59 * mm});
            skCircle(sketch, "E11.0.2.57", {"center": v(311.15, 25.4) * mm, "radius": 1.59 * mm});
            skCircle(sketch, "E11.0.2.58", {"center": v(295.28, 25.4) * mm, "radius": 1.59 * mm});
            skCircle(sketch, "E11.0.2.59", {"center": v(136.53, 25.4) * mm, "radius": 1.59 * mm});
            skCircle(sketch, "E11.0.2.60", {"center": v(107.95, 19.05) * mm, "radius": 1.59 * mm});
            skCircle(sketch, "E11.0.2.61", {"center": v(260.35, 38.1) * mm, "radius": 1.59 * mm});
            skCircle(sketch, "E11.0.2.62", {"center": v(231.78, 38.1) * mm, "radius": 1.59 * mm});
            skCircle(sketch, "E11.0.2.63", {"center": v(184.15, 25.4) * mm, "radius": 1.59 * mm});
            skCircle(sketch, "E11.0.2.64", {"center": v(336.55, 25.4) * mm, "radius": 1.59 * mm});
            skCircle(sketch, "E11.0.2.65", {"center": v(282.58, 25.4) * mm, "radius": 1.59 * mm});
            skCircle(sketch, "E11.0.2.66", {"center": v(161.92, 25.4) * mm, "radius": 1.59 * mm});
            skCircle(sketch, "E11.0.2.67", {"center": v(212.73, 19.05) * mm, "radius": 1.59 * mm});
            skCircle(sketch, "E11.0.2.68", {"center": v(184.15, 19.05) * mm, "radius": 1.59 * mm});
            skCircle(sketch, "E11.0.2.69", {"center": v(323.85, 38.1) * mm, "radius": 1.59 * mm});
            skCircle(sketch, "E11.0.2.70", {"center": v(225.43, 25.4) * mm, "radius": 1.59 * mm});
            skCircle(sketch, "E11.0.2.71", {"center": v(196.85, 19.05) * mm, "radius": 1.59 * mm});
            skCircle(sketch, "E11.0.2.72", {"center": v(149.22, 38.1) * mm, "radius": 1.59 * mm});
            skCircle(sketch, "E11.0.2.73", {"center": v(336.55, 31.75) * mm, "radius": 1.59 * mm});
            skCircle(sketch, "E11.0.2.74", {"center": v(295.28, 31.75) * mm, "radius": 1.59 * mm});
            skCircle(sketch, "E11.0.2.75", {"center": v(241.3, 25.4) * mm, "radius": 1.59 * mm});
            skCircle(sketch, "E11.0.2.76", {"center": v(114.3, 25.4) * mm, "radius": 1.59 * mm});
            skCircle(sketch, "E11.0.2.77", {"center": v(212.73, 25.4) * mm, "radius": 1.59 * mm});
            skCircle(sketch, "E11.0.2.78", {"center": v(171.45, 19.05) * mm, "radius": 1.59 * mm});
            skCircle(sketch, "E11.0.2.79", {"center": v(336.55, 38.1) * mm, "radius": 1.59 * mm});
            skCircle(sketch, "E11.0.2.80", {"center": v(288.93, 25.4) * mm, "radius": 1.59 * mm});
            skCircle(sketch, "E11.0.2.81", {"center": v(266.7, 25.4) * mm, "radius": 1.59 * mm});
            skCircle(sketch, "E11.0.2.82", {"center": v(190.5, 38.1) * mm, "radius": 1.59 * mm});
            skCircle(sketch, "E11.0.2.83", {"center": v(161.92, 38.1) * mm, "radius": 1.59 * mm});
            skCircle(sketch, "E11.0.2.84", {"center": v(317.5, 19.05) * mm, "radius": 1.59 * mm});
            skCircle(sketch, "E11.0.2.85", {"center": v(288.93, 19.05) * mm, "radius": 1.59 * mm});
            skCircle(sketch, "E11.0.2.86", {"center": v(254, 38.1) * mm, "radius": 1.59 * mm});
            skCircle(sketch, "E11.0.2.87", {"center": v(330.2, 25.4) * mm, "radius": 1.59 * mm});
            skCircle(sketch, "E11.0.2.88", {"center": v(301.63, 19.05) * mm, "radius": 1.59 * mm});
            skCircle(sketch, "E11.0.2.89", {"center": v(266.7, 31.75) * mm, "radius": 1.59 * mm});
            skCircle(sketch, "E11.0.2.90", {"center": v(120.65, 31.75) * mm, "radius": 1.59 * mm});
            skCircle(sketch, "E11.0.2.91", {"center": v(171.45, 31.75) * mm, "radius": 1.59 * mm});
            skLineSegment(sketch, "E11.0.2.92", {"start": v(114.3, 31.75) * mm, "end": v(149.22, 31.75) * mm, "construction": true});
            skCircle(sketch, "E11.0.2.93", {"center": v(247.65, 19.05) * mm, "radius": 1.59 * mm});
            skCircle(sketch, "E11.0.2.94", {"center": v(127, 38.1) * mm, "radius": 1.59 * mm});
            skCircle(sketch, "E11.0.2.95", {"center": v(247.65, 25.4) * mm, "radius": 1.59 * mm});
            skCircle(sketch, "E11.0.2.96", {"center": v(127, 31.75) * mm, "radius": 1.59 * mm});
            skCircle(sketch, "E11.0.2.97", {"center": v(225.43, 38.1) * mm, "radius": 1.59 * mm});
            skCircle(sketch, "E11.0.2.98", {"center": v(282.58, 38.1) * mm, "radius": 1.59 * mm});
            skCircle(sketch, "E11.0.2.99", {"center": v(260.35, 31.75) * mm, "radius": 1.59 * mm});
            skCircle(sketch, "E11.0.2.100", {"center": v(212.73, 31.75) * mm, "radius": 1.59 * mm});
            skCircle(sketch, "E11.0.2.101", {"center": v(219.08, 31.75) * mm, "radius": 1.59 * mm});
            skCircle(sketch, "E11.0.2.102", {"center": v(301.63, 31.75) * mm, "radius": 1.59 * mm});
            skCircle(sketch, "E11.0.2.103", {"center": v(212.73, 38.1) * mm, "radius": 1.59 * mm});
            skCircle(sketch, "E11.0.2.104", {"center": v(323.85, 31.75) * mm, "radius": 1.59 * mm});
            skCircle(sketch, "E11.0.2.105", {"center": v(142.88, 31.75) * mm, "radius": 1.59 * mm});
            skCircle(sketch, "E11.0.2.106", {"center": v(149.22, 31.75) * mm, "radius": 1.59 * mm});
            skCircle(sketch, "E11.0.2.107", {"center": v(107.95, 25.4) * mm, "radius": 1.59 * mm});
            skCircle(sketch, "E11.0.2.108", {"center": v(247.65, 31.75) * mm, "radius": 1.59 * mm});
            skCircle(sketch, "E11.0.2.109", {"center": v(254, 31.75) * mm, "radius": 1.59 * mm});
            skCircle(sketch, "E11.0.2.110", {"center": v(295.28, 19.05) * mm, "radius": 1.59 * mm});
            skCircle(sketch, "E11.0.2.111", {"center": v(114.3, 31.75) * mm, "radius": 1.59 * mm});
            skCircle(sketch, "E11.0.2.112", {"center": v(241.3, 31.75) * mm, "radius": 1.59 * mm});
            skCircle(sketch, "E11.0.2.113", {"center": v(161.92, 31.75) * mm, "radius": 1.59 * mm});
            skCircle(sketch, "E11.0.2.114", {"center": v(114.3, 19.05) * mm, "radius": 1.59 * mm});
            skCircle(sketch, "E11.0.2.115", {"center": v(225.43, 19.05) * mm, "radius": 1.59 * mm});
            skCircle(sketch, "E11.0.2.116", {"center": v(120.65, 38.1) * mm, "radius": 1.59 * mm});
            skCircle(sketch, "E11.0.2.117", {"center": v(225.43, 31.75) * mm, "radius": 1.59 * mm});
            skCircle(sketch, "E11.0.2.118", {"center": v(177.8, 31.75) * mm, "radius": 1.59 * mm});
            skCircle(sketch, "E11.0.2.119", {"center": v(184.15, 31.75) * mm, "radius": 1.59 * mm});
            skCircle(sketch, "E11.0.2.120", {"center": v(142.88, 19.05) * mm, "radius": 1.59 * mm});
            skLineSegment(sketch, "E11.0.2.121", {"start": v(171.45, 38.1) * mm, "end": v(171.45, 31.75) * mm, "construction": true});
            skCircle(sketch, "E11.0.2.122", {"center": v(177.8, 38.1) * mm, "radius": 1.59 * mm});
            skCircle(sketch, "E11.0.2.123", {"center": v(171.45, 38.1) * mm, "radius": 1.59 * mm});
            skCircle(sketch, "E11.0.2.124", {"center": v(276.23, 31.75) * mm, "radius": 1.59 * mm});
            skCircle(sketch, "E11.0.2.125", {"center": v(101.6, 31.75) * mm, "radius": 1.59 * mm});
            skLineSegment(sketch, "E11.0.2.126", {"start": v(171.45, 38.1) * mm, "end": v(177.8, 38.1) * mm, "construction": true});
            skLineSegment(sketch, "E11.0.2.127", {"start": v(276.23, 38.1) * mm, "end": v(276.23, 31.75) * mm, "construction": true});
            skCircle(sketch, "E11.0.2.128", {"center": v(206.38, 31.75) * mm, "radius": 1.59 * mm});
            skCircle(sketch, "E11.0.2.129", {"center": v(276.23, 38.1) * mm, "radius": 1.59 * mm});
            skLineSegment(sketch, "E11.0.2.130", {"start": v(276.23, 38.1) * mm, "end": v(282.58, 38.1) * mm, "construction": true});
            skCircle(sketch, "E11.0.2.131", {"center": v(107.95, 38.1) * mm, "radius": 1.59 * mm});
            skCircle(sketch, "E11.0.2.132", {"center": v(107.95, 31.75) * mm, "radius": 1.59 * mm});
            skCircle(sketch, "E11.0.2.133", {"center": v(317.5, 31.75) * mm, "radius": 1.59 * mm});
            skCircle(sketch, "E11.0.2.134", {"center": v(206.38, 38.1) * mm, "radius": 1.59 * mm});
            skCircle(sketch, "E11.0.2.135", {"center": v(311.15, 31.75) * mm, "radius": 1.59 * mm});
            skCircle(sketch, "E11.0.2.136", {"center": v(136.53, 31.75) * mm, "radius": 1.59 * mm});
            skLineSegment(sketch, "E11.0.2.137", {"start": v(206.38, 38.1) * mm, "end": v(212.72, 38.1) * mm, "construction": true});
            skCircle(sketch, "E11.0.2.138", {"center": v(317.5, 38.1) * mm, "radius": 1.59 * mm});
            skCircle(sketch, "E11.0.2.139", {"center": v(142.88, 38.1) * mm, "radius": 1.59 * mm});
            skCircle(sketch, "E11.0.2.140", {"center": v(114.3, 38.1) * mm, "radius": 1.59 * mm});
            skLineSegment(sketch, "E11.0.2.141", {"start": v(311.15, 38.1) * mm, "end": v(311.15, 31.75) * mm, "construction": true});
            skCircle(sketch, "E11.0.2.142", {"center": v(311.15, 38.1) * mm, "radius": 1.59 * mm});
            skCircle(sketch, "E11.0.2.143", {"center": v(247.65, 38.1) * mm, "radius": 1.59 * mm});
            skLineSegment(sketch, "E11.0.2.144", {"start": v(311.15, 38.1) * mm, "end": v(317.5, 38.1) * mm, "construction": true});
            skLineSegment(sketch, "E11.0.2.145", {"start": v(241.3, 38.1) * mm, "end": v(241.3, 31.75) * mm, "construction": true});
            skCircle(sketch, "E11.0.2.146", {"center": v(241.3, 38.1) * mm, "radius": 1.59 * mm});
            skLineSegment(sketch, "E11.0.2.147", {"start": v(241.3, 38.1) * mm, "end": v(247.65, 38.1) * mm, "construction": true});
            skCircle(sketch, "E11.0.2.148", {"center": v(101.6, 38.1) * mm, "radius": 1.59 * mm});
            skLineSegment(sketch, "E11.0.2.149", {"start": v(101.6, 38.1) * mm, "end": v(107.95, 38.1) * mm, "construction": true});
            skLineSegment(sketch, "E11.0.2.150", {"start": v(101.6, 38.1) * mm, "end": v(101.6, 31.75) * mm, "construction": true});
            skLineSegment(sketch, "E11.0.2.151", {"start": v(206.38, 38.1) * mm, "end": v(206.38, 31.75) * mm, "construction": true});
            skLineSegment(sketch, "E11.0.2.152", {"start": v(136.53, 38.1) * mm, "end": v(136.53, 31.75) * mm, "construction": true});
            skCircle(sketch, "E11.0.2.153", {"center": v(136.53, 38.1) * mm, "radius": 1.59 * mm});
            skLineSegment(sketch, "E11.0.2.154", {"start": v(136.53, 38.1) * mm, "end": v(142.87, 38.1) * mm, "construction": true});
            skLineSegment(sketch, "E11.direction1", {"start": v(219.08, 107.95) * mm, "end": v(244.48, 107.95) * mm, "construction": true});
            skLineSegment(sketch, "E11.direction2", {"start": v(219.08, 107.95) * mm, "end": v(219.08, 66.68) * mm, "construction": true});
            skCircle(sketch, "E12", {"center": v(346.07, 120.65) * mm, "radius": 1.59 * mm});
            skLineSegment(sketch, "E13", {"start": v(419.1, 69.85) * mm, "end": v(346.07, 69.85) * mm});
            skLineSegment(sketch, "E14", {"start": v(346.07, 120.65) * mm, "end": v(346.07, 0) * mm});
            skCircle(sketch, "E15", {"center": v(346.07, 114.3) * mm, "radius": 1.59 * mm});
            skCircle(sketch, "E16", {"center": v(346.07, 107.95) * mm, "radius": 1.59 * mm});
            skCircle(sketch, "E17", {"center": v(346.07, 101.6) * mm, "radius": 1.59 * mm});
            skCircle(sketch, "E18.1.0", {"center": v(356.93, 99.69) * mm, "radius": 1.59 * mm});
            skCircle(sketch, "E18.1.1", {"center": v(359.1, 105.65) * mm, "radius": 1.59 * mm});
            skCircle(sketch, "E18.1.2", {"center": v(361.28, 111.62) * mm, "radius": 1.59 * mm});
            skCircle(sketch, "E18.1.3", {"center": v(363.45, 117.59) * mm, "radius": 1.59 * mm});
            skCircle(sketch, "E18.2.0", {"center": v(366.48, 94.17) * mm, "radius": 1.59 * mm});
            skCircle(sketch, "E18.2.1", {"center": v(370.57, 99.04) * mm, "radius": 1.59 * mm});
            skCircle(sketch, "E18.2.2", {"center": v(374.65, 103.9) * mm, "radius": 1.59 * mm});
            skCircle(sketch, "E18.2.3", {"center": v(378.73, 108.77) * mm, "radius": 1.59 * mm});
            skCircle(sketch, "E18.3.0", {"center": v(373.57, 85.73) * mm, "radius": 1.59 * mm});
            skCircle(sketch, "E18.3.1", {"center": v(379.07, 88.9) * mm, "radius": 1.59 * mm});
            skCircle(sketch, "E18.3.2", {"center": v(384.57, 92.08) * mm, "radius": 1.59 * mm});
            skCircle(sketch, "E18.3.3", {"center": v(390.07, 95.25) * mm, "radius": 1.59 * mm});
            skCircle(sketch, "E18.4.0", {"center": v(377.34, 75.36) * mm, "radius": 1.59 * mm});
            skCircle(sketch, "E18.4.1", {"center": v(383.6, 76.47) * mm, "radius": 1.59 * mm});
            skCircle(sketch, "E18.4.2", {"center": v(389.85, 77.57) * mm, "radius": 1.59 * mm});
            skCircle(sketch, "E18.4.3", {"center": v(396.1, 78.67) * mm, "radius": 1.59 * mm});
            skCircle(sketch, "E18.5.0", {"center": v(377.34, 64.34) * mm, "radius": 1.59 * mm});
            skCircle(sketch, "E18.5.1", {"center": v(383.6, 63.23) * mm, "radius": 1.59 * mm});
            skCircle(sketch, "E18.5.2", {"center": v(389.85, 62.13) * mm, "radius": 1.59 * mm});
            skCircle(sketch, "E18.5.3", {"center": v(396.1, 61.03) * mm, "radius": 1.59 * mm});
            skCircle(sketch, "E18.6.0", {"center": v(373.57, 53.97) * mm, "radius": 1.59 * mm});
            skCircle(sketch, "E18.6.1", {"center": v(379.07, 50.8) * mm, "radius": 1.59 * mm});
            skCircle(sketch, "E18.6.2", {"center": v(384.57, 47.63) * mm, "radius": 1.59 * mm});
            skCircle(sketch, "E18.6.3", {"center": v(390.07, 44.45) * mm, "radius": 1.59 * mm});
            skCircle(sketch, "E18.7.0", {"center": v(366.48, 45.53) * mm, "radius": 1.59 * mm});
            skCircle(sketch, "E18.7.1", {"center": v(370.57, 40.66) * mm, "radius": 1.59 * mm});
            skCircle(sketch, "E18.7.2", {"center": v(374.65, 35.8) * mm, "radius": 1.59 * mm});
            skCircle(sketch, "E18.7.3", {"center": v(378.73, 30.93) * mm, "radius": 1.59 * mm});
            skCircle(sketch, "E18.8.0", {"center": v(356.93, 40.01) * mm, "radius": 1.59 * mm});
            skCircle(sketch, "E18.8.1", {"center": v(359.1, 34.05) * mm, "radius": 1.59 * mm});
            skCircle(sketch, "E18.8.2", {"center": v(361.28, 28.08) * mm, "radius": 1.59 * mm});
            skCircle(sketch, "E18.8.3", {"center": v(363.45, 22.11) * mm, "radius": 1.59 * mm});
            skCircle(sketch, "E18.9.0", {"center": v(346.07, 38.1) * mm, "radius": 1.59 * mm});
            skCircle(sketch, "E18.9.1", {"center": v(346.07, 31.75) * mm, "radius": 1.59 * mm});
            skCircle(sketch, "E18.9.2", {"center": v(346.07, 25.4) * mm, "radius": 1.59 * mm});
            skCircle(sketch, "E18.9.3", {"center": v(346.07, 19.05) * mm, "radius": 1.59 * mm});
            skPoint(sketch, "E18.center", {"position": v(346.07, 69.85) * mm});
            skLineSegment(sketch, "E18.anchor1", {"start": v(346.07, 69.85) * mm, "end": v(346.07, 101.6) * mm, "construction": true});
            skLineSegment(sketch, "E18.anchor2", {"start": v(346.07, 69.85) * mm, "end": v(346.07, 38.1) * mm, "construction": true});
            skCircle(sketch, "E19", {"center": v(92.07, 19.05) * mm, "radius": 1.59 * mm});
            skCircle(sketch, "E20", {"center": v(92.07, 25.4) * mm, "radius": 1.59 * mm});
            skCircle(sketch, "E21", {"center": v(92.07, 31.75) * mm, "radius": 1.59 * mm});
            skCircle(sketch, "E22", {"center": v(92.07, 38.1) * mm, "radius": 1.59 * mm});
            skLineSegment(sketch, "E23", {"start": v(92.07, 38.1) * mm, "end": v(92.07, 49.21) * mm});
            skCircle(sketch, "E24.1.0", {"center": v(84.22, 41.35) * mm, "radius": 1.59 * mm});
            skCircle(sketch, "E24.1.1", {"center": v(79.73, 36.86) * mm, "radius": 1.59 * mm});
            skCircle(sketch, "E24.1.2", {"center": v(75.24, 32.37) * mm, "radius": 1.59 * mm});
            skCircle(sketch, "E24.1.3", {"center": v(70.75, 27.88) * mm, "radius": 1.59 * mm});
            skCircle(sketch, "E24.2.0", {"center": v(80.96, 49.21) * mm, "radius": 1.59 * mm});
            skCircle(sketch, "E24.2.1", {"center": v(74.61, 49.21) * mm, "radius": 1.59 * mm});
            skCircle(sketch, "E24.2.2", {"center": v(68.26, 49.21) * mm, "radius": 1.59 * mm});
            skCircle(sketch, "E24.2.3", {"center": v(61.91, 49.21) * mm, "radius": 1.59 * mm});
            skCircle(sketch, "E24.3.0", {"center": v(84.22, 57.07) * mm, "radius": 1.59 * mm});
            skCircle(sketch, "E24.3.1", {"center": v(79.73, 61.56) * mm, "radius": 1.59 * mm});
            skCircle(sketch, "E24.3.2", {"center": v(75.24, 66.05) * mm, "radius": 1.59 * mm});
            skCircle(sketch, "E24.3.3", {"center": v(70.75, 70.54) * mm, "radius": 1.59 * mm});
            skCircle(sketch, "E24.4.0", {"center": v(92.07, 60.33) * mm, "radius": 1.59 * mm});
            skCircle(sketch, "E24.4.1", {"center": v(92.07, 66.68) * mm, "radius": 1.59 * mm});
            skCircle(sketch, "E24.4.2", {"center": v(92.07, 73.03) * mm, "radius": 1.59 * mm});
            skCircle(sketch, "E24.4.3", {"center": v(92.07, 79.38) * mm, "radius": 1.59 * mm});
            skPoint(sketch, "E24.center", {"position": v(92.07, 49.21) * mm});
            skLineSegment(sketch, "E24.anchor1", {"start": v(92.07, 49.21) * mm, "end": v(92.07, 38.1) * mm, "construction": true});
            skLineSegment(sketch, "E24.anchor2", {"start": v(92.07, 49.21) * mm, "end": v(92.07, 60.33) * mm, "construction": true});
            skCircle(sketch, "E25", {"center": v(355.6, 69.85) * mm, "radius": 1.59 * mm});
            skSolve(sketch);
        }
        {
            var Q0;
            Q0 = qSketchRegion(id + "F2", true);
            extrude(context, id + "F3", {"entities" : qUnion([Q0]), "operationType" : NewBodyOperationType.REMOVE, "oppositeDirection" : true, "depth" : 12.7 * mm});
        }
    });
